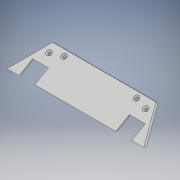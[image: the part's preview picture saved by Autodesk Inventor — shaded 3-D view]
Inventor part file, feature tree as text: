
AUTODESK INVENTOR PART (.ipt)
format: ipt  version: 2019 (Build 230136000, 136)  size: 156,672 bytes
history: native  units: mm
features: chamfer x4, extrude x3, sketch x3, other x1
ambient origin geometry x8: Origin, YZ Plane, XZ Plane, XY Plane, X Axis, Y Axis, Z Axis, Center Point
bodies: Body1 (feature_tree)
feature tree (11):
  other  "Bryła1"
  extrude  "Wyciągnięcie proste1"  Depth=2.0mm
  extrude  "Wyciągnięcie proste2"  Depth=22.0mm
  extrude  "Wyciągnięcie proste3"  TaperAngle=30.0deg  [1 undecoded]
  chamfer  "Faza1"  Distance=180.175mm
  chamfer  "Faza2"  Distance=2.0mm
  chamfer  "Faza3"  Angle=45.0deg  [1 undecoded]
  chamfer  "Faza4"  Distance=180.175mm
  sketch  "Szkic1"
  sketch  "Szkic2"
  sketch  "Szkic3"
note: 2 required parameter values undecoded (feature->parameter linkage not recoverable at this tier; creation-order binding heuristic only, values carry confidence <= 0.55)
